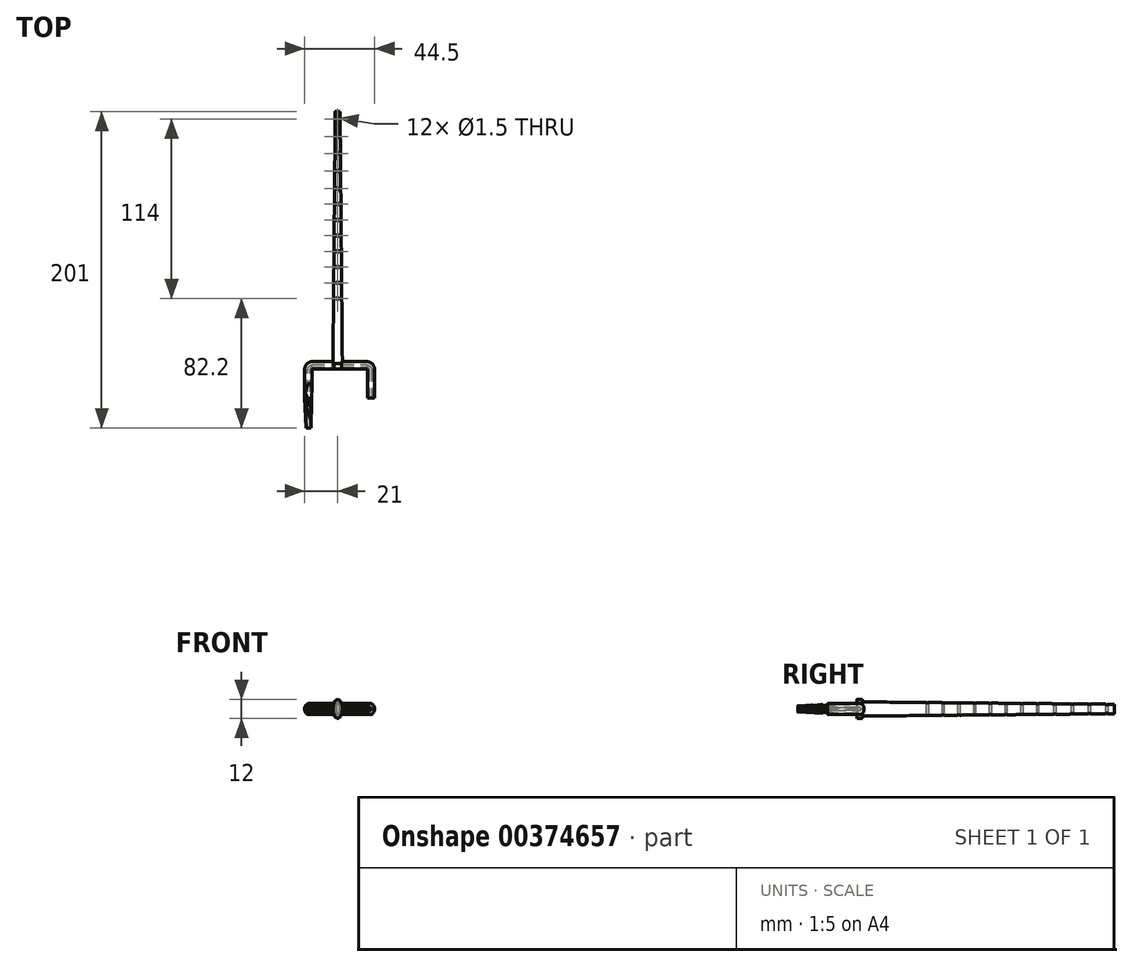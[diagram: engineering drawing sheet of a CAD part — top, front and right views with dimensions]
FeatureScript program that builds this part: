
annotation { "Feature Type Name" : "Feature", "Feature Type Description" : "" }
export const myFeature = defineFeature(function(context is Context, id is Id, definition is map)
    precondition{}
    {
        {
            var Q0;
            Q0=qCreatedBy(makeId("Front.planeOp"),FACE);
            var sketch = newSketch(context, id + "F0", { "sketchPlane" : qUnion([Q0])});
            skArc(sketch, "E0", {"start": v(0.49, 0.84) * mm, "mid": v(-0.97, 0) * mm, "end": v(0.49, -0.84) * mm});
            skLineSegment(sketch, "E1", {"start": v(0.49, 0.84) * mm, "end": v(1.68, 2.9) * mm});
            skLineSegment(sketch, "E2", {"start": v(0.49, -0.84) * mm, "end": v(1.68, -2.9) * mm});
            skEllipticalArc(sketch, "E3", {});
            const initialGuessF0  = {"E3": [0, 0, -1, 0, 0.003, 0.0035, 4.1196187055742195, 2.1635666016053645]};
            skSetInitialGuess(sketch, initialGuessF0);
            skSolve(sketch);
        }
        {
            var Q0;
            Q0=qCreatedBy(makeId("Top.planeOp"),FACE);
            var sketch = newSketch(context, id + "F1", { "sketchPlane" : qUnion([Q0])});
            skLineSegment(sketch, "E4", {"start": v(0, 0) * mm, "end": v(0, 37) * mm});
            skArc(sketch, "E5", {"start": v(0, 37) * mm, "mid": v(0.64, 38.56) * mm, "end": v(2.2, 39.2) * mm});
            skLineSegment(sketch, "E6", {"start": v(2.2, 39.2) * mm, "end": v(36.3, 39.2) * mm});
            skArc(sketch, "E7", {"start": v(38.5, 37) * mm, "mid": v(37.86, 38.56) * mm, "end": v(36.3, 39.2) * mm});
            skLineSegment(sketch, "E8", {"start": v(38.5, 37) * mm, "end": v(38.5, 19) * mm});
            skSolve(sketch);
        }
        {
            var Q0;
            Q0=qSketchRegion(id+"F0",true);
            var Q1;
            Q1=qConstructionFilter(qBodyType(qCreatedBy(id+"F0",EDGE),BodyType.WIRE),ConstructionObject.NO);
            var Q2;
            Q2=qConstructionFilter(qBodyType(qCreatedBy(id+"F1",EDGE),BodyType.WIRE),ConstructionObject.NO);
            sweep(context, id + "F2", {"profiles" : qUnion([Q0]), "surfaceProfiles" : qUnion([Q1]), "path" : qUnion([Q2])});
        }
        {
            var Q0;
            Q0=qCreatedBy(makeId("Right.planeOp"),FACE);
            var sketch = newSketch(context, id + "F3", { "sketchPlane" : qUnion([Q0])});
            skLineSegment(sketch, "E9", {"start": v(0, 2) * mm, "end": v(28.41, 3.5) * mm});
            skLineSegment(sketch, "E10", {"start": v(-1.87, 2) * mm, "end": v(0, 2) * mm});
            skLineSegment(sketch, "E11", {"start": v(-4.03, 0) * mm, "end": v(22.25, 0) * mm, "construction": true});
            skLineSegment(sketch, "E12", {"start": v(28.41, 3.5) * mm, "end": v(28.41, 8.2) * mm});
            skLineSegment(sketch, "E13", {"start": v(28.41, 8.2) * mm, "end": v(-1.87, 8.2) * mm});
            skLineSegment(sketch, "E14", {"start": v(-1.87, 8.2) * mm, "end": v(-1.87, 2) * mm});
            skSolve(sketch);
        }
        {
            var Q0;
            Q0=makeQuery(id+"F3.imprint","IMPRINT",FACE,{"disambiguationData":[TD([[makeQuery(id+"F3.imprint","IMPRINT",EDGE,{"derivedFrom":sQuery(id+"F3.wireOp",EDGE,"E9")}),1.0]])]});
            var Q1;
            Q1=sQuery(id+"F3.wireOp",EDGE,"E11");
            revolve(context, id + "F4", {"operationType" : NewBodyOperationType.REMOVE, "entities" : qUnion([Q0]), "axis" : qUnion([Q1]), "revolveType" : RevolveType.FULL, "oppositeDirection" : true});
        }
        {
            var Q0;
            Q0=qCreatedBy(makeId("Top.planeOp"),FACE);
            cPlane(context, id + "F5", {"entities" : qUnion([Q0]), "cplaneType" : CPlaneType.OFFSET, "offset" : 10 * mm, "width" : 150 * mm, "height" : 150 * mm});
        }
        {
            var Q0;
            Q0=qCreatedBy(id+"F5.planeOp",FACE);
            var sketch = newSketch(context, id + "F6", { "sketchPlane" : qUnion([Q0])});
            skLineSegment(sketch, "E15", {"start": v(1.23, 4) * mm, "end": v(-4.27, 20.45) * mm});
            skLineSegment(sketch, "E16", {"start": v(-4.27, 20.45) * mm, "end": v(-1.9, 21.25) * mm});
            skLineSegment(sketch, "E17", {"start": v(-1.9, 21.25) * mm, "end": v(3.75, 4.36) * mm});
            skLineSegment(sketch, "E18", {"start": v(3.75, 4.36) * mm, "end": v(1.23, 4) * mm});
            skLineSegment(sketch, "E19", {"start": v(-4.35, 16) * mm, "end": v(7.78, 16) * mm, "construction": true});
            skLineSegment(sketch, "E20", {"start": v(-5.1, 4) * mm, "end": v(7.56, 4) * mm, "construction": true});
            skSolve(sketch);
        }
        {
            var Q0;
            Q0 = qSketchRegion(id + "F6", true);
            extrude(context, id + "F7", {"entities" : qUnion([Q0]), "operationType" : NewBodyOperationType.REMOVE, "oppositeDirection" : true, "depth" : 8 * mm, "offsetDistance" : 25 * mm});
        }
        {
            var Q0;
            Q0=qCreatedBy(makeId("Right.planeOp"),FACE);
            var sketch = newSketch(context, id + "F8", { "sketchPlane" : qUnion([Q0])});
            skLineSegment(sketch, "E21.bottom", {"start": v(15.6, 2.23) * mm, "end": v(18.6, 2.23) * mm});
            skLineSegment(sketch, "E21.top", {"start": v(15.6, 4.52) * mm, "end": v(18.6, 4.52) * mm});
            skLineSegment(sketch, "E21.left", {"start": v(15.6, 2.23) * mm, "end": v(15.6, 4.52) * mm});
            skLineSegment(sketch, "E21.right", {"start": v(18.6, 2.23) * mm, "end": v(18.6, 4.52) * mm});
            skLineSegment(sketch, "E22.bottom", {"start": v(15.6, -2.04) * mm, "end": v(18.6, -2.04) * mm});
            skLineSegment(sketch, "E22.top", {"start": v(15.6, -3.78) * mm, "end": v(18.6, -3.78) * mm});
            skLineSegment(sketch, "E22.left", {"start": v(15.6, -2.04) * mm, "end": v(15.6, -3.78) * mm});
            skLineSegment(sketch, "E22.right", {"start": v(18.6, -2.04) * mm, "end": v(18.6, -3.78) * mm});
            skSolve(sketch);
        }
        {
            var Q0;
            Q0 = qSketchRegion(id + "F8", true);
            extrude(context, id + "F9", {"entities" : qUnion([Q0]), "operationType" : NewBodyOperationType.REMOVE, "oppositeDirection" : true, "depth" : 3 * mm, "offsetDistance" : 25 * mm, "hasSecondDirection" : true, "secondDirectionOppositeDirection" : false, "secondDirectionDepth" : 5 * mm});
        }
        {
            var Q0;
            Q0=makeQuery(id+"F2.opSweep","CAP_FACE",FACE,{"disambiguationData":[OSD([sQuery(id+"F0.wireOp",EDGE,"E0"),sQuery(id+"F0.wireOp",EDGE,"E1"),sQuery(id+"F0.wireOp",EDGE,"E2"),sQuery(id+"F0.wireOp",EDGE,"E3"),sQuery(id+"F1.wireOp",VERTEX,"E8.end")])],"isStart":false});
            cPlane(context, id + "F10", {"entities" : qUnion([Q0]), "cplaneType" : CPlaneType.OFFSET, "offset" : 22 * mm, "oppositeDirection" : true, "width" : 150 * mm, "height" : 150 * mm});
        }
        {
            var Q0;
            Q0=qCreatedBy(id+"F10.planeOp",FACE);
            var sketch = newSketch(context, id + "F11", { "sketchPlane" : qUnion([Q0])});
            skEllipse(sketch, "E23", {"center": v(18, 0) * mm, "majorRadius": 4.5 * mm, "minorRadius": 3 * mm, "majorAxis": v(0, -1)});
            skSolve(sketch);
        }
        {
            var Q0;
            Q0 = qSketchRegion(id + "F11", true);
            extrude(context, id + "F12", {"entities" : qUnion([Q0]), "operationType" : NewBodyOperationType.ADD, "oppositeDirection" : true, "depth" : 160 * mm, "offsetDistance" : 25 * mm, "hasDraft" : true, "draftAngle" : 0.53 * degree, "draftPullDirection" : true});
        }
        {
            var Q0;
            Q0=makeQuery(id+"F12.boolean.opBoolean","SPLIT",FACE,{"disambiguationData":[OD(1.0)],"derivedFrom":makeQuery(id+"F12.opExtrude","CAP_FACE",FACE,{"disambiguationData":[OSD([sQuery(id+"F11.wireOp",EDGE,"E23")])],"isStart":true})});
            var sketch = newSketch(context, id + "F13", { "sketchPlane" : qUnion([Q0])});
            skFitSpline(sketch, "E24.0.0", {"points": [v(18, 6) * mm, v(17.8, 6) * mm, v(17.6, 5.96) * mm, v(17.22, 5.8) * mm, v(17.03, 5.7) * mm, v(16.67, 5.4) * mm, v(16.5, 5.2) * mm, v(16.17, 4.77) * mm, v(16.02, 4.52) * mm, v(15.74, 3.96) * mm, v(15.61, 3.66) * mm, v(15.4, 3) * mm, v(15.3, 2.66) * mm, v(15.08, 1.57) * mm, v(15, 0.79) * mm, v(15, -0.79) * mm, v(15.08, -1.57) * mm, v(15.3, -2.66) * mm, v(15.4, -3) * mm, v(15.61, -3.66) * mm, v(15.74, -3.96) * mm, v(16.02, -4.52) * mm, v(16.17, -4.77) * mm, v(16.5, -5.2) * mm, v(16.67, -5.4) * mm, v(17.03, -5.7) * mm, v(17.22, -5.8) * mm, v(17.6, -5.96) * mm, v(17.8, -6) * mm, v(18, -6) * mm, v(18.2, -6) * mm, v(18.4, -5.96) * mm, v(18.78, -5.8) * mm, v(18.97, -5.7) * mm, v(19.33, -5.4) * mm, v(19.5, -5.2) * mm, v(19.83, -4.77) * mm, v(19.98, -4.52) * mm, v(20.26, -3.96) * mm, v(20.39, -3.66) * mm, v(20.6, -3) * mm, v(20.7, -2.66) * mm, v(20.92, -1.57) * mm, v(21, -0.79) * mm, v(21, 0.79) * mm, v(20.92, 1.57) * mm, v(20.7, 2.66) * mm, v(20.6, 3) * mm, v(20.39, 3.66) * mm, v(20.26, 3.96) * mm, v(19.98, 4.52) * mm, v(19.83, 4.77) * mm, v(19.5, 5.2) * mm, v(19.33, 5.4) * mm, v(18.97, 5.7) * mm, v(18.78, 5.8) * mm, v(18.4, 5.96) * mm, v(18.2, 6) * mm, v(18, 6) * mm]});
            skLineSegment(sketch, "E24.0.1", {"start": v(15.65, 2.8) * mm, "end": v(20.35, 2.8) * mm});
            skFitSpline(sketch, "E25.0.0", {"points": [v(18, 6) * mm, v(17.8, 6) * mm, v(17.6, 5.96) * mm, v(17.22, 5.8) * mm, v(17.03, 5.7) * mm, v(16.67, 5.4) * mm, v(16.5, 5.2) * mm, v(16.17, 4.77) * mm, v(16.02, 4.52) * mm, v(15.74, 3.96) * mm, v(15.61, 3.66) * mm, v(15.4, 3) * mm, v(15.3, 2.66) * mm, v(15.08, 1.57) * mm, v(15, 0.79) * mm, v(15, -0.79) * mm, v(15.08, -1.57) * mm, v(15.3, -2.66) * mm, v(15.4, -3) * mm, v(15.61, -3.66) * mm, v(15.74, -3.96) * mm, v(16.02, -4.52) * mm, v(16.17, -4.77) * mm, v(16.5, -5.2) * mm, v(16.67, -5.4) * mm, v(17.03, -5.7) * mm, v(17.22, -5.8) * mm, v(17.6, -5.96) * mm, v(17.8, -6) * mm, v(18, -6) * mm, v(18.2, -6) * mm, v(18.4, -5.96) * mm, v(18.78, -5.8) * mm, v(18.97, -5.7) * mm, v(19.33, -5.4) * mm, v(19.5, -5.2) * mm, v(19.83, -4.77) * mm, v(19.98, -4.52) * mm, v(20.26, -3.96) * mm, v(20.39, -3.66) * mm, v(20.6, -3) * mm, v(20.7, -2.66) * mm, v(20.92, -1.57) * mm, v(21, -0.79) * mm, v(21, 0.79) * mm, v(20.92, 1.57) * mm, v(20.7, 2.66) * mm, v(20.6, 3) * mm, v(20.39, 3.66) * mm, v(20.26, 3.96) * mm, v(19.98, 4.52) * mm, v(19.83, 4.77) * mm, v(19.5, 5.2) * mm, v(19.33, 5.4) * mm, v(18.97, 5.7) * mm, v(18.78, 5.8) * mm, v(18.4, 5.96) * mm, v(18.2, 6) * mm, v(18, 6) * mm]});
            skLineSegment(sketch, "E25.0.1", {"start": v(20.35, -2.8) * mm, "end": v(15.65, -2.8) * mm});
            skSolve(sketch);
        }
        {
            var Q0;
            Q0 = qSketchRegion(id + "F13", true);
            extrude(context, id + "F14", {"entities" : qUnion([Q0]), "operationType" : NewBodyOperationType.ADD, "depth" : 3.5 * mm, "offsetDistance" : 25 * mm});
        }
        {
            var Q0;
            Q0=qCreatedBy(makeId("Top.planeOp"),FACE);
            var sketch = newSketch(context, id + "F15", { "sketchPlane" : qUnion([Q0])});
            skLineSegment(sketch, "E26", {"start": v(18, 36.53) * mm, "end": v(18, 48.98) * mm, "construction": true});
            skCircle(sketch, "E27", {"center": v(18, 152.2) * mm, "radius": 0.75 * mm});
            skCircle(sketch, "E28.0.1.0", {"center": v(18, 142.2) * mm, "radius": 0.75 * mm});
            skCircle(sketch, "E28.0.2.0", {"center": v(18, 132.2) * mm, "radius": 0.75 * mm});
            skCircle(sketch, "E28.0.3.0", {"center": v(18, 122.2) * mm, "radius": 0.75 * mm});
            skCircle(sketch, "E28.0.4.0", {"center": v(18, 112.2) * mm, "radius": 0.75 * mm});
            skCircle(sketch, "E28.0.5.0", {"center": v(18, 102.2) * mm, "radius": 0.75 * mm});
            skCircle(sketch, "E28.0.6.0", {"center": v(18, 92.2) * mm, "radius": 0.75 * mm});
            skCircle(sketch, "E28.0.7.0", {"center": v(18, 82.2) * mm, "radius": 0.75 * mm});
            skLineSegment(sketch, "E28.direction1", {"start": v(18, 152.2) * mm, "end": v(-7, 152.2) * mm, "construction": true});
            skLineSegment(sketch, "E28.direction2", {"start": v(18, 152.2) * mm, "end": v(18, 142.2) * mm, "construction": true});
            skCircle(sketch, "E29.0.1.0", {"center": v(18, 163.2) * mm, "radius": 0.75 * mm});
            skCircle(sketch, "E29.0.2.0", {"center": v(18, 174.2) * mm, "radius": 0.75 * mm});
            skCircle(sketch, "E29.0.3.0", {"center": v(18, 185.2) * mm, "radius": 0.75 * mm});
            skCircle(sketch, "E29.0.4.0", {"center": v(18, 196.2) * mm, "radius": 0.75 * mm});
            skLineSegment(sketch, "E29.direction1", {"start": v(18, 152.2) * mm, "end": v(43, 152.2) * mm, "construction": true});
            skLineSegment(sketch, "E29.direction2", {"start": v(18, 152.2) * mm, "end": v(18, 163.2) * mm, "construction": true});
            skSolve(sketch);
        }
        {
            var Q0;
            Q0 = qSketchRegion(id + "F15", true);
            extrude(context, id + "F16", {"entities" : qUnion([Q0]), "operationType" : NewBodyOperationType.REMOVE, "endBound" : BoundingType.THROUGH_ALL, "depth" : 25 * mm, "offsetDistance" : 25 * mm});
        }
        {
            var Q0;
            Q0 = qSketchRegion(id + "F15", true);
            extrude(context, id + "F17", {"entities" : qUnion([Q0]), "operationType" : NewBodyOperationType.REMOVE, "oppositeDirection" : true, "depth" : 25 * mm, "offsetDistance" : 25 * mm});
        }
    });
